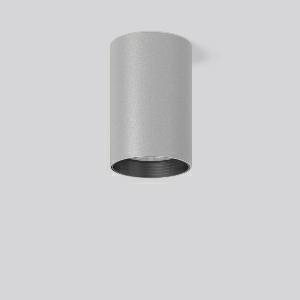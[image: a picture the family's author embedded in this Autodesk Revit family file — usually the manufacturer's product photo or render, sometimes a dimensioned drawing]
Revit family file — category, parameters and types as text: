
# Revit family: heledon_maxi_a_931228_004_2_fc1e
name_source: partatom
category: Lighting Fixtures
units: mm (PartAtom-declared; Revit-internal decimal feet)

## family parameters
Cut with Voids When Loaded = No
Host = Face
Light Source = No
Part Type = Normal
Room Calculation Point = No
Round Connector Dimension = Use Diameter
Shared = No

## types (1)
- HELEDON maxi A (1 x LED Modul 927, 3350 lm, 2700)
    Apparent Load = 35 VA
    Approval mark = CE
    CIE Flux Codes = 96 100 100 100 100
    Color Rendering = 92
    Color Temperature = 2700
    Default Elevation = 1800 mm
    Description = Series: HELEDON maxi
Cylindrical surface-mounted downlight. Housing: die-cast aluminium, powder-coated. Internal ceiling frame polycarbonate with bayonet mounting. Black plastic ring and recessed LED to prevent glare from the side. Optical assembly with lens made of plastic (polycarbonate) for the best homogeneous light distribution - can be changed without tools. Best colour rendering index Ra>90. Suitable for Ceiling mounting. Easy installation with a separate ceiling frame with bayonet mounting and plug connection. Driver integrated. Connected via plug-in connector. High quality converter without flickering and stroboscopic effect. The following accessories can be mounted without use of tools: interchangeable lenses, decorative glasses, honeycomb louvre, clear and frosted diffusers, white interchangeable plastic ring. 
Colour: silver
Diameter: 123 mm
Height: 183 mm
Lamp: LED
Socket: without socket
Colour temperature: 2700K
Colour rendering index (CRI): 92
System power: 35 W
Rated luminous flux: 3350 lm
Luminous efficiency: 96 lm/W
Control gear: Regulated power supply
Protection class: I
Type of protection: IP 20
    Height = 183 mm
    Lamp = 1 x LED Modul 927
    Lamp Light Flux = 3350 lm
    Lamp count = 1
    Length = 123 mm
    Lifetime = 50000 h
    Luminous efficacy = 96 lm/W
    Manufacturer = RZB
    ModVariant = No
    Model = 931228.004.2
    Mounting Place = Ceiling
    Mounting Type = Surface mounted
    Number of Poles = 1
    OnlyDefault = Yes
    Power Factor = 1
    Product Name = HELEDON maxi A
    Product group = Surface mounted downlights
    ProductGroupID = 302
    Protection Class = Protection class I
    Protection Degree = IP 20
    RLX_Detail_Level = 1
    RLX_Emergency_Light_Flux = 0 lm
    RLX_Emergency_Type = 0
    RLX_Emergency_Type_DB = No
    RlxData = <blob elided: 98797 chars, md5=5c0d5108>
    Socket = socket
    Standby Power = 0 W
    System Light Flux = 3350 lm
    System Power = 35 W
    Type Comments = Product without accessories
    Type Image = 931193.004.jpg
    URL = http://relux.com
    VarID = ---
    Voltage = 230 V
    Voltage Range = 220-240 V
    Weight = 0.00 kg
    Width = 0 mm  [stored 0 ft]

note: [stored X ft] marks values corroborated as IEEE doubles in the binary element streams (Revit-internal decimal feet)

## geometry (parser evidence)
native form markers: Blend x4, Sweep x12
no freeform markers — native parametric forms only
